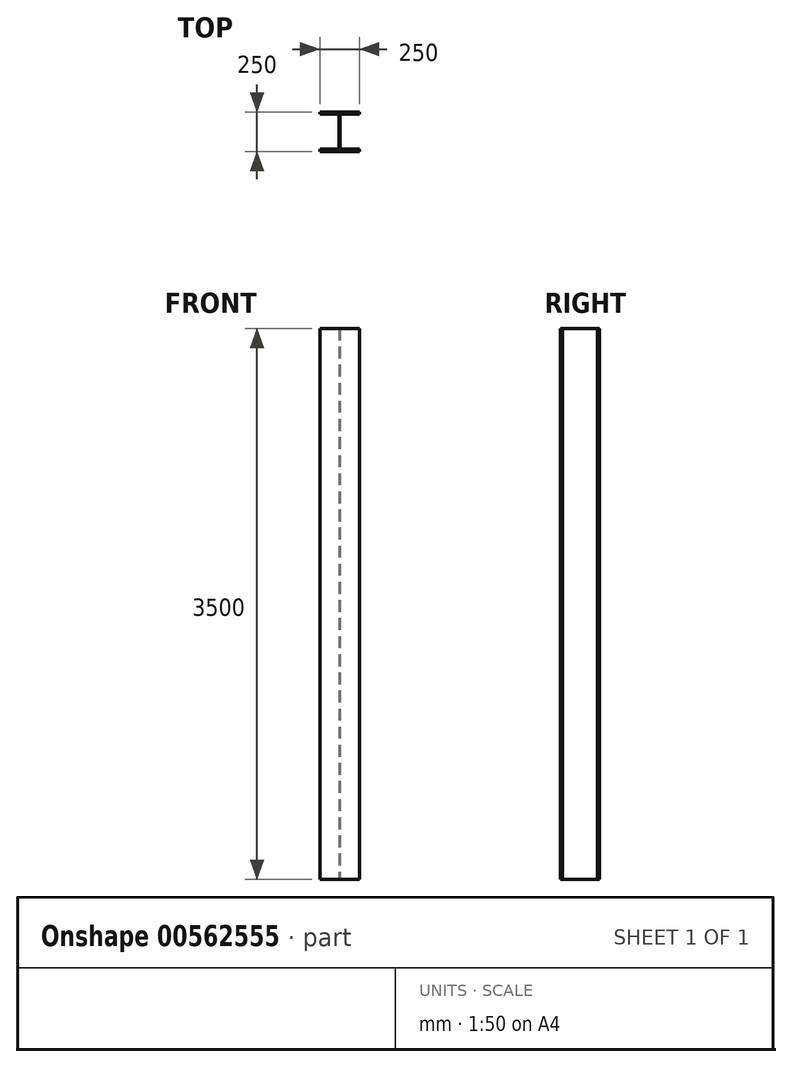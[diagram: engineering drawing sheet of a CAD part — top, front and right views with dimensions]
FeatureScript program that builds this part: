
annotation { "Feature Type Name" : "Feature", "Feature Type Description" : "" }
export const myFeature = defineFeature(function(context is Context, id is Id, definition is map)
    precondition{}
    {
        {
            var Q0;
            Q0=qCreatedBy(makeId("Top.planeOp"),FACE);
            var sketch = newSketch(context, id + "F0", { "sketchPlane" : qUnion([Q0])});
            skLineSegment(sketch, "E0", {"start": v(0, 250) * mm, "end": v(-125, 250) * mm});
            skLineSegment(sketch, "E1", {"start": v(-125, 250) * mm, "end": v(-125, 236) * mm});
            skLineSegment(sketch, "E2", {"start": v(-125, 236) * mm, "end": v(-4, 236) * mm});
            skLineSegment(sketch, "E3", {"start": v(-4, 236) * mm, "end": v(-4, 14) * mm});
            skLineSegment(sketch, "E4", {"start": v(-4, 14) * mm, "end": v(-125, 14) * mm});
            skLineSegment(sketch, "E5", {"start": v(-125, 14) * mm, "end": v(-125, 0) * mm});
            skLineSegment(sketch, "E6", {"start": v(-125, 0) * mm, "end": v(0, 0) * mm});
            skLineSegment(sketch, "E7.MirrorCS", {"start": v(125, 236) * mm, "end": v(4, 236) * mm});
            skLineSegment(sketch, "E8.MirrorCS", {"start": v(125, 0) * mm, "end": v(0, 0) * mm});
            skLineSegment(sketch, "E9.MirrorCS", {"start": v(125, 250) * mm, "end": v(125, 236) * mm});
            skLineSegment(sketch, "E10.MirrorCS", {"start": v(4, 14) * mm, "end": v(125, 14) * mm});
            skLineSegment(sketch, "E11.MirrorCS", {"start": v(0, 250) * mm, "end": v(125, 250) * mm});
            skLineSegment(sketch, "E12.MirrorCS", {"start": v(4, 236) * mm, "end": v(4, 14) * mm});
            skLineSegment(sketch, "E13.MirrorCS", {"start": v(125, 14) * mm, "end": v(125, 0) * mm});
            skSolve(sketch);
        }
        {
            var Q0;
            Q0=makeQuery(id+"F0.imprint","IMPRINT",FACE,{"disambiguationData":[TD([[makeQuery(id+"F0.imprint","IMPRINT",EDGE,{"derivedFrom":sQuery(id+"F0.wireOp",EDGE,"E0")}),1.0]])]});
            var Q1;
            Q1=makeQuery(id+"F0.imprint","IMPRINT",FACE,{"disambiguationData":[TD([[makeQuery(id+"F0.imprint","IMPRINT",EDGE,{"derivedFrom":sQuery(id+"F0.wireOp",EDGE,"E7.MirrorCS")}),-1.0]])]});
            extrude(context, id + "F1", {"entities" : qUnion([Q0, Q1]), "depth" : 3500 * mm, "offsetDistance" : 25 * mm});
        }
    });
